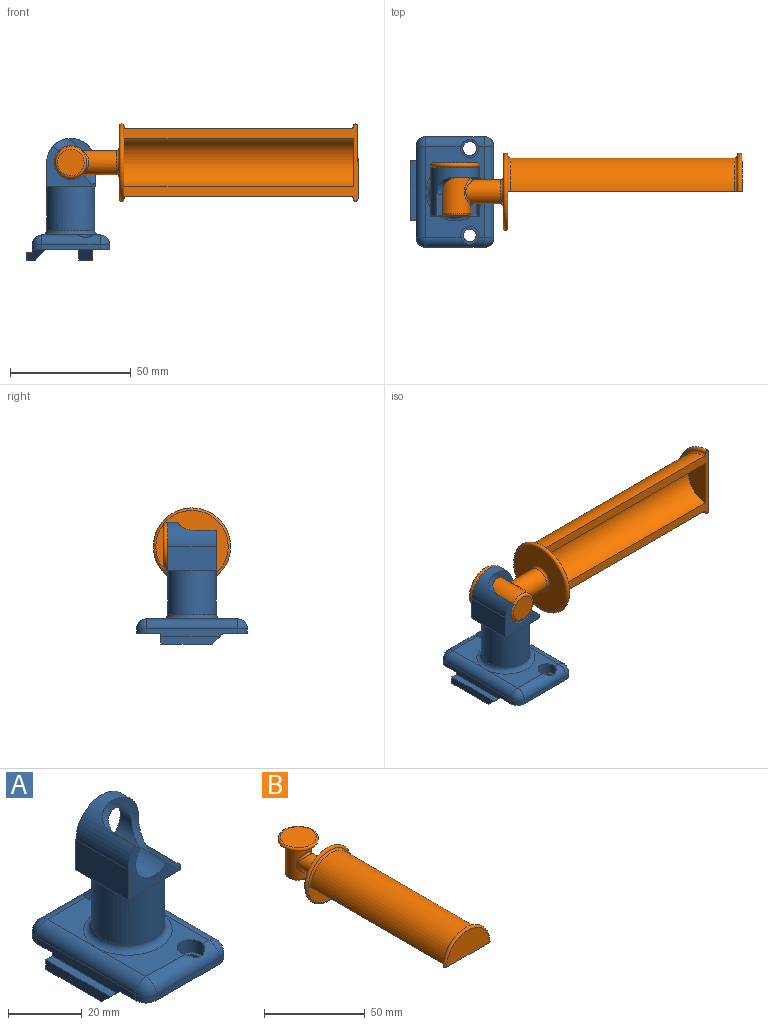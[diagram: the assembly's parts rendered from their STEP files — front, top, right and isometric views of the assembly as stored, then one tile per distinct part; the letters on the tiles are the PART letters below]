
ASSEMBLY  parts=2 mates=1
PART A: 56 faces, bbox 34.7x46x52.3 mm
  f0: cylinder r=10mm len=20mm, axis (0,1,0), area 253.7mm2, adj f23,f24,f25,f26,f45,f46,f49
  f1: cylinder r=2.93mm len=5.86mm, axis (0,0,-1), area 32.2mm2, adj f14,f20
  f2: cylinder r=2.62mm len=5.25mm, axis (0,0,-1), area 28.9mm2, adj f14,f18
  f3: plane 8.3x4.39mm, normal (0,1,0), area 24mm2, adj f6,f7,f8,f9,f10,f14
  f4: plane 38x2mm, normal (1,0,0), area 76mm2, adj f14,f37,f41,f43
  f5: plane 38x24.2mm, normal (0,0,1), area 408.2mm2, adj f19,f21,f35,f36,f40,f41,f44
  f6: plane 38x3.14mm, normal (-1,0,0), area 104.9mm2, adj f3,f7,f14,f32,f34,f35,f51
  f7: plane 24.75x2.5mm, normal (0,0,1), area 61.9mm2, adj f3,f6,f8,f51
  f8: plane 24.75x3.25mm, normal (-1,0,0), area 75.2mm2, adj f3,f7,f9,f51
  f9: plane 21.5x3.91mm, normal (0,0,-1), area 84.1mm2, adj f3,f8,f10,f51
  f10: plane 25.89x4.39mm, normal (0.71,0,-0.71), area 147.1mm2, adj f3,f9,f14,f51
  f11: plane 25.89x4.39mm, normal (-1,0,0), area 104mm2, adj f12,f14,f15,f52
  f12: plane 21.5x5.86mm, normal (0,0,-1), area 126mm2, adj f11,f13,f15,f52
  f13: plane 25.89x4.39mm, normal (1,0,0), area 104mm2, adj f12,f14,f15,f52
  f14: plane 46x32.2mm, normal (0,0,-1), area 1117mm2, adj f1,f2,f3,f4,f6,f10,f11,f13
  f15: plane 5.86x4.39mm, normal (0,1,0), area 25.7mm2, adj f11,f12,f13,f14
  f16: plane 24.2x2mm, normal (0,1,0), area 48.4mm2, adj f14,f32,f36,f37
  f17: plane 24.2x2mm, normal (0,-1,0), area 48.4mm2, adj f14,f34,f40,f43
  f18: plane 7.5x7.5mm, normal (0,0,1), area 22.5mm2, adj f2,f19
  f19: cylinder r=3.75mm len=7.5mm, axis (0,0,1), area 94.9mm2, adj f5,f18,f40
  f20: plane 7.5x7.5mm, normal (0,0,1), area 17.2mm2, adj f1,f21
  f21: cylinder r=3.75mm len=7.5mm, axis (0,0,1), area 94.9mm2, adj f5,f20,f36
  f22: cylinder r=10mm len=20mm, axis (0,0,-1), area 1131mm2, adj f27,f28,f29,f30,f44
  f23: plane 20x20mm, normal (0,1,0), area 203.1mm2, adj f0,f25,f26,f27,f30,f31
  f24: plane 20x16.69mm, normal (0,-1,0), area 110.6mm2, adj f0,f25,f26,f28,f29,f31,f45,f47
  f25: plane 20x10mm, normal (-1,0,0), area 200mm2, adj f0,f23,f24,f29,f30
  f26: plane 20x10mm, normal (1,0,0), area 73.8mm2, adj f0,f23,f24,f27,f28,f46,f48,f50
  f27: plane 10x10mm, normal (0,0,-1), area 21.5mm2, adj f22,f23,f26
  f28: plane 10x10mm, normal (0,0,-1), area 21.5mm2, adj f22,f24,f26
  f29: plane 10x10mm, normal (0,0,-1), area 21.5mm2, adj f22,f24,f25
  f30: plane 10x10mm, normal (0,0,-1), area 21.5mm2, adj f22,f23,f25
  f31: cylinder r=7mm len=20mm, axis (0,-1,0), area 542.2mm2, adj f23,f24,f45,f46,f47,f49,f50
  f32: cylinder r=4mm len=4mm, axis (0,0,1), area 12.6mm2, adj f6,f14,f16,f33
  f33: sphere r=4mm, area 25.1mm2, adj f32,f35,f36
  f34: cylinder r=4mm len=4mm, axis (0,0,1), area 12.6mm2, adj f6,f14,f17,f38
  f35: cylinder r=4mm len=38mm, axis (0,-1,0), area 238.8mm2, adj f5,f6,f33,f38
  f36: cylinder r=4mm len=24.2mm, axis (1,0,0), area 136.3mm2, adj f5,f16,f21,f33,f39
  f37: cylinder r=4mm len=4mm, axis (0,0,-1), area 12.6mm2, adj f4,f14,f16,f39
  f38: sphere r=4mm, area 25.1mm2, adj f34,f35,f40
  f39: sphere r=4mm, area 25.1mm2, adj f36,f37,f41
  f40: cylinder r=4mm len=24.2mm, axis (1,0,0), area 136.3mm2, adj f5,f17,f19,f38,f42
  f41: cylinder r=4mm len=38mm, axis (0,1,0), area 238.8mm2, adj f4,f5,f39,f42
  f42: sphere r=4mm, area 25.1mm2, adj f40,f41,f43
  f43: cylinder r=4mm len=4mm, axis (0,0,-1), area 12.6mm2, adj f4,f14,f17,f42
  f44: torus R=12mm, axis (0,0,-1), area 211.7mm2, adj f5,f22
  f45: plane 9x2.23mm, normal (0.67,0,0.74), area 27mm2, adj f0,f24,f31,f49
  f46: plane 10.62x10.28mm, normal (0,-1,0), area 31.3mm2, adj f0,f26,f31,f49,f50
  f47: plane 9x4.32mm, normal (0.72,0,0.69), area 54mm2, adj f24,f31,f48,f50
  f48: cylinder r=13mm len=13.23mm, axis (0,-1,0), area 16.9mm2, adj f24,f26,f47,f50
  f49: cylinder r=7mm len=12.12mm, axis (0.74,0,-0.67), area 37.5mm2, adj f0,f31,f45,f46
  f50: cylinder r=7mm len=14.21mm, axis (0.69,0,-0.72), area 59.2mm2, adj f26,f31,f46,f47,f48
  f51: plane 8.3x4.39mm, normal (0,-0.71,-0.71), area 33.9mm2, adj f6,f7,f8,f9,f10,f14
  f52: plane 5.86x4.39mm, normal (0,-0.71,-0.71), area 36.4mm2, adj f11,f12,f13,f14
  f53: plane 14x14mm, normal (0,0,1), area 153.9mm2, adj f54
  f54: cylinder r=7mm len=20mm, axis (0,0,-1), area 879.6mm2, adj f53,f55
  f55: plane 14x14mm, normal (0,0,-1), area 153.9mm2, adj f54
PART B: 24 faces, bbox 34.6x129.8x34.6 mm
  f0: plane 30x25mm, normal (0,-1,0), area 510.5mm2, adj f7,f8,f14
  f1: cylinder r=6.5mm len=18mm, axis (0,0,-1), area 626.3mm2, adj f16,f19,f20
  f2: plane 11x11mm, normal (0,0,-1), area 95mm2, adj f19
  f3: plane 18x18mm, normal (0,0,1), area 254.5mm2, adj f18
  f4: plane 18x18mm, normal (0,0,-1), area 77.8mm2, adj f18,f20
  f5: cylinder r=5mm len=14.5mm, axis (0,1,0), area 405.5mm2, adj f16,f17
  f6: plane 30x30mm, normal (0,1,0), area 593.8mm2, adj f14,f17
  f7: cylinder r=10mm len=95mm, axis (0,1,0), area 2984.5mm2, adj f0,f8,f10
  f8: plane 97x32mm, normal (0,0,-1), area 824mm2, adj f0,f7,f9,f10,f11,f12,f13,f15
  f9: cylinder r=14mm len=93mm, axis (0,1,0), area 4090.4mm2, adj f8,f12,f15
  f10: plane 20x10mm, normal (0,1,0), area 157.1mm2, adj f7,f8
  f11: plane 30x15mm, normal (0,-1,0), area 353.4mm2, adj f8,f13
  f12: torus R=15mm, axis (0,-1,0), area 70.9mm2, adj f8,f9,f13
  f13: torus R=15mm, axis (0,-1,0), area 154.3mm2, adj f8,f11,f12
  f14: torus R=15mm, axis (0,-1,0), area 308.7mm2, adj f0,f6,f15
  f15: torus R=15mm, axis (0,-1,0), area 70.9mm2, adj f8,f9,f14
  f16: bspline ~12.01x10.41mm, area 39mm2, adj f1,f5
  f17: torus R=6mm, axis (0,-1,0), area 52.9mm2, adj f5,f6
  f18: torus R=9mm, axis (0,0,1), area 190.2mm2, adj f3,f4
  f19: torus R=5.5mm, axis (0,0,1), area 60.6mm2, adj f1,f2
  f20: torus R=7.5mm, axis (0,0,1), area 67.7mm2, adj f1,f4
  f21: cylinder r=6.5mm len=6mm, axis (0,0,-1), area 29.1mm2, adj f22
  f22: cylinder r=3mm len=14.23mm, axis (0,-1,0), area 261.3mm2, adj f21,f23
  f23: plane 6x6mm, normal (0,1,0), area 28.3mm2, adj f22
PLACE A t=(9.8,-7.19,-7.16)mm fixed
PLACE B rot(axis=(-0.58,0.58,0.58),120deg) t=(20.1,-20.19,28.84)mm
MATE revolute A.f0 <-> B.f1  axis (0,-1,0) through (20.1,-20.19,28.84)mm
